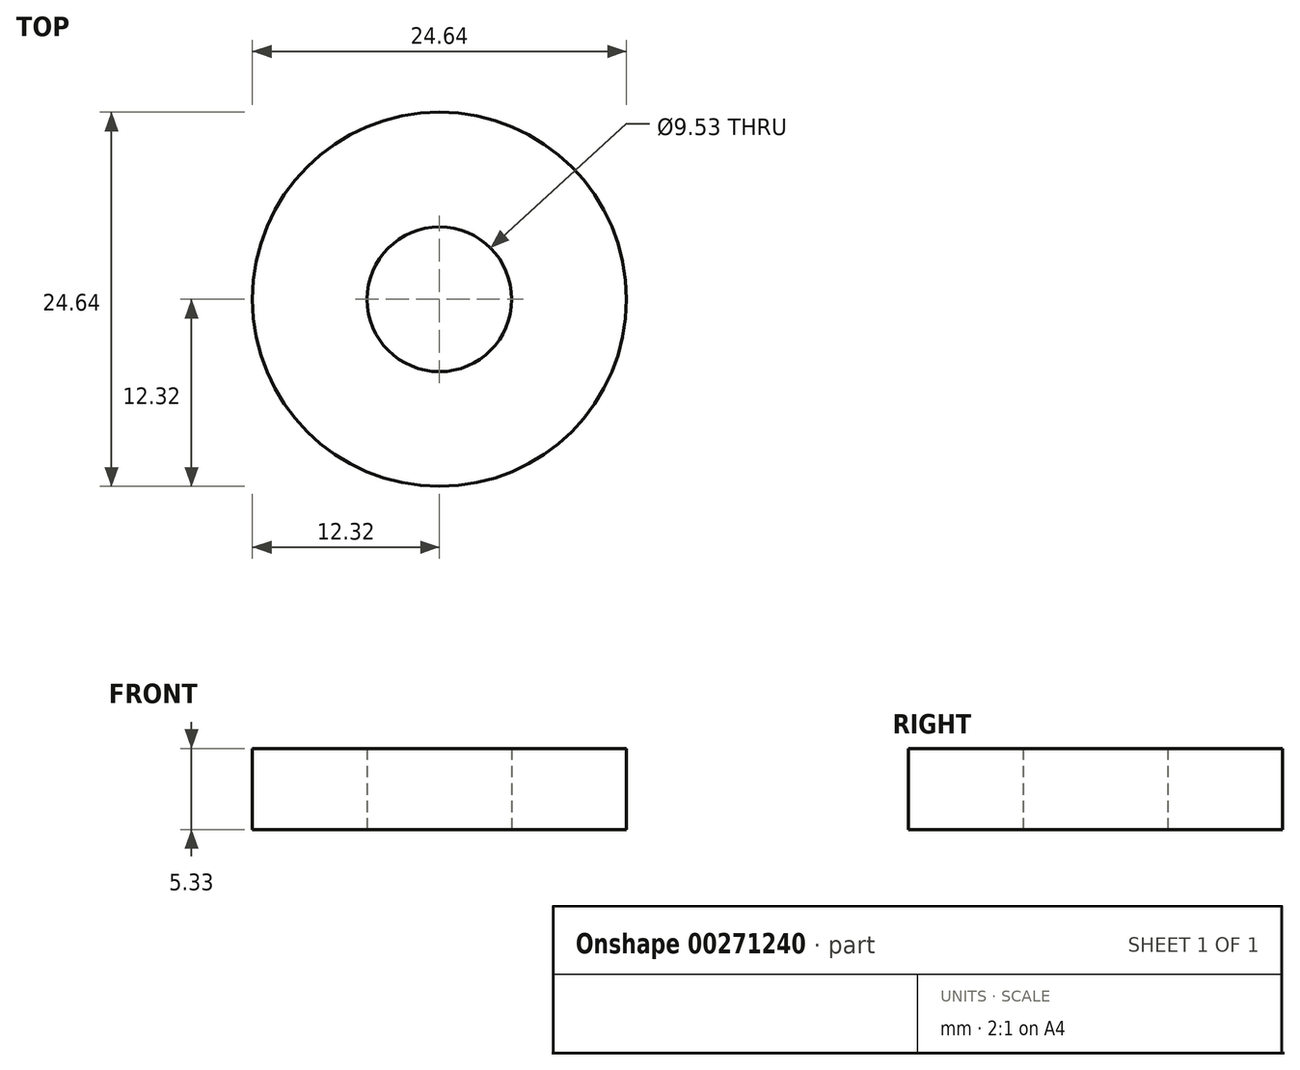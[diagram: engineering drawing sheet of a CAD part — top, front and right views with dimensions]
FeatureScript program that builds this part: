
annotation { "Feature Type Name" : "Feature", "Feature Type Description" : "" }
export const myFeature = defineFeature(function(context is Context, id is Id, definition is map)
    precondition{}
    {
        {
            var Q0;
            Q0=qCreatedBy(makeId("Top.planeOp"),FACE);
            var sketch = newSketch(context, id + "F0", { "sketchPlane" : qUnion([Q0])});
            skCircle(sketch, "E0", {"center": v(0, 0) * mm, "radius": 12.32 * mm});
            skCircle(sketch, "E1", {"center": v(0, 0) * mm, "radius": 4.76 * mm});
            skSolve(sketch);
        }
        {
            var Q0;
            Q0 = qSketchRegion(id + "F0", true);
            extrude(context, id + "F1", {"entities" : qUnion([Q0]), "depth" : 5.33 * mm});
        }
    });
